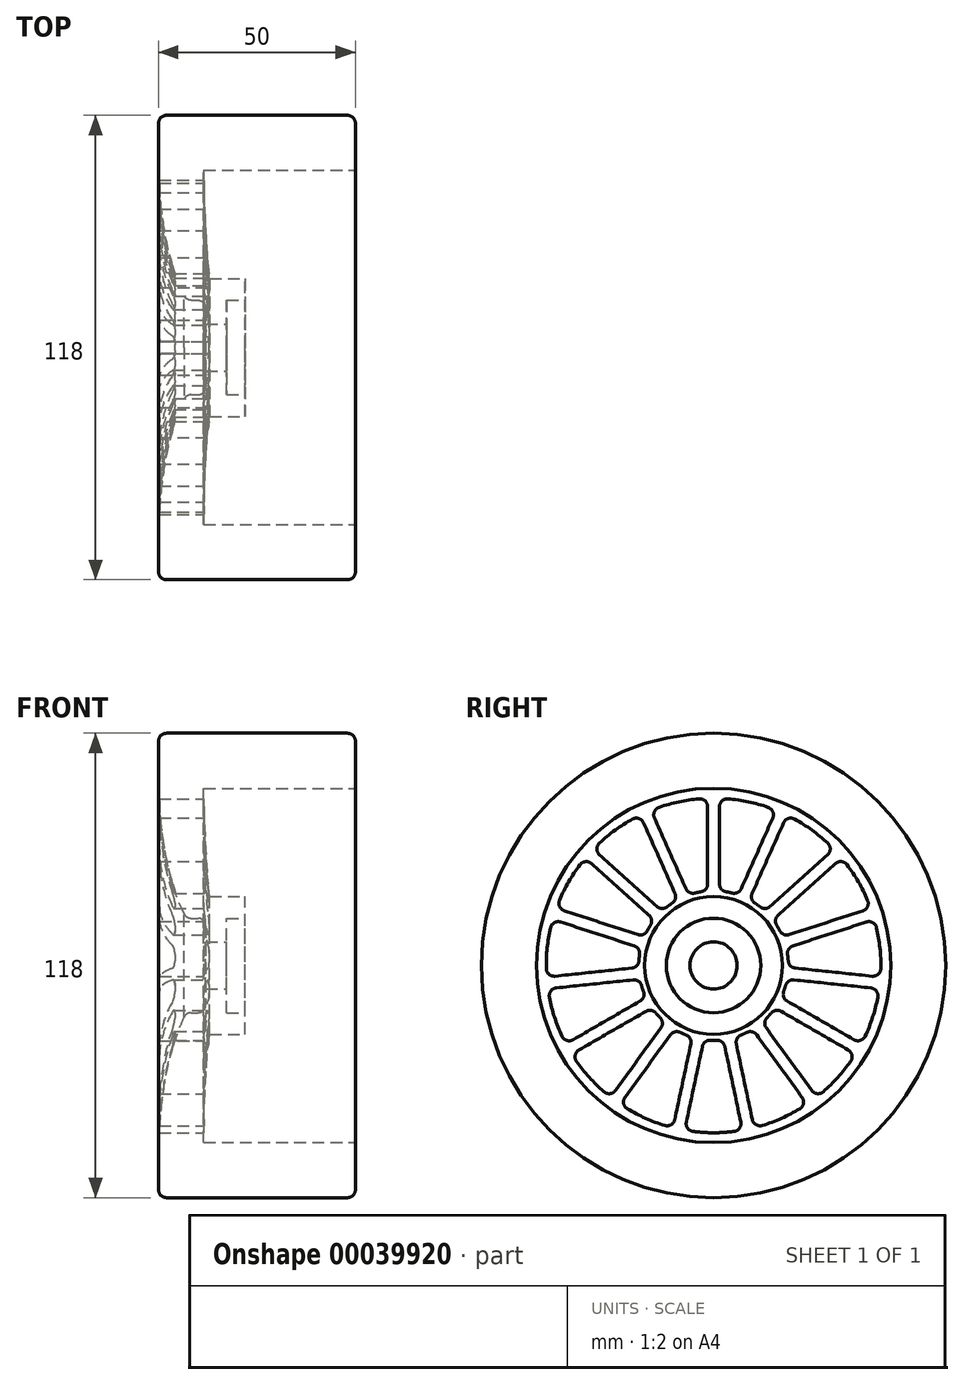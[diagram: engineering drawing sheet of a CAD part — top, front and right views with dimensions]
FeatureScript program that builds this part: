
annotation { "Feature Type Name" : "Feature", "Feature Type Description" : "" }
export const myFeature = defineFeature(function(context is Context, id is Id, definition is map)
    precondition{}
    {
        {
            var Q0;
            Q0=qCreatedBy(makeId("Right.planeOp"),FACE);
            var sketch = newSketch(context, id + "F0", { "sketchPlane" : qUnion([Q0]), "disableImprinting" : false});
            skCircle(sketch, "E0", {"center": v(0, 0) * mm, "radius": 59 * mm});
            skCircle(sketch, "E1", {"center": v(0, 0) * mm, "radius": 49 * mm});
            skSolve(sketch);
        }
        {
            var Q0;
            Q0=makeQuery(id+"F0.imprint","IMPRINT",FACE,{"disambiguationData":[TD([[makeQuery(id+"F0.imprint","IMPRINT",EDGE,{"derivedFrom":sQuery(id+"F0.wireOp",EDGE,"E0")}),1.0]])]});
            extrude(context, id + "F1", {"entities" : qUnion([Q0]), "oppositeDirection" : true, "depth" : 50 * mm});
        }
        {
            var Q0;
            Q0=qCreatedBy(makeId("Front.planeOp"),FACE);
            var sketch = newSketch(context, id + "F2", { "sketchPlane" : qUnion([Q0])});
            skLineSegment(sketch, "E2.bottom", {"start": v(0, 0) * mm, "end": v(-50, 0) * mm});
            skLineSegment(sketch, "E2.left", {"start": v(0, 0) * mm, "end": v(0, 49) * mm});
            skLineSegment(sketch, "E2.right", {"start": v(-50, 0) * mm, "end": v(-50, 49) * mm});
            skLineSegment(sketch, "E3", {"start": v(-50, 0) * mm, "end": v(-43, 0) * mm});
            skLineSegment(sketch, "E4", {"start": v(-50, 49) * mm, "end": v(0, 49) * mm});
            skLineSegment(sketch, "E5", {"start": v(0, 49) * mm, "end": v(0, 45) * mm});
            skLineSegment(sketch, "E6", {"start": v(-43, 0) * mm, "end": v(-43, 12) * mm, "construction": true});
            skLineSegment(sketch, "E7", {"start": v(-43, 12) * mm, "end": v(-38, 12) * mm});
            skFitSpline(sketch, "E8", {"points": [v(-43, 12) * mm, v(-50, 49) * mm], "startDerivative": vector(-8.6, 17.02) * mm, "endDerivative": vector(0, 58.5) * mm});
            skLineSegment(sketch, "E9", {"start": v(0, 45) * mm, "end": v(-38.53, 45) * mm});
            skLineSegment(sketch, "E10", {"start": v(0, 0) * mm, "end": v(0, 17.5) * mm});
            skLineSegment(sketch, "E11", {"start": v(0, 17.5) * mm, "end": v(-37, 17.5) * mm, "construction": true});
            skLineSegment(sketch, "E12", {"start": v(-38, 12) * mm, "end": v(-37, 12) * mm});
            skLineSegment(sketch, "E13", {"start": v(-37, 12) * mm, "end": v(-37, 17.5) * mm, "construction": true});
            skFitSpline(sketch, "E14", {"points": [v(-38.53, 45) * mm, v(-37, 17.5) * mm], "startDerivative": vector(0, -29.52) * mm, "endDerivative": vector(1.96, -9.49) * mm});
            skLineSegment(sketch, "E15", {"start": v(-38.53, 45) * mm, "end": v(-38.53, 35.16) * mm, "construction": true});
            skLineSegment(sketch, "E16", {"start": v(-38, 12) * mm, "end": v(-38, 6) * mm});
            skLineSegment(sketch, "E17", {"start": v(-38, 6) * mm, "end": v(-32.68, 6) * mm});
            skLineSegment(sketch, "E18", {"start": v(-32.68, 6) * mm, "end": v(-32.68, 12) * mm});
            skLineSegment(sketch, "E19", {"start": v(-32.68, 12) * mm, "end": v(-28.02, 12) * mm});
            skLineSegment(sketch, "E20", {"start": v(-28.02, 12) * mm, "end": v(-28.02, 17.5) * mm});
            skLineSegment(sketch, "E21", {"start": v(-28.02, 17.5) * mm, "end": v(-37, 17.5) * mm});
            skPoint(sketch, "E22.orphan", {"position": v(-50, 59) * mm});
            skPoint(sketch, "E23.orphan", {"position": v(0, 59) * mm});
            skSolve(sketch);
        }
        {
            var Q0;
            Q0=qCreatedBy(makeId("Front.planeOp"),FACE);
            var sketch = newSketch(context, id + "F3", { "sketchPlane" : qUnion([Q0])});
            skLineSegment(sketch, "E24", {"start": v(-51.75, 0) * mm, "end": v(-81.76, 0) * mm, "construction": true});
            skSolve(sketch);
        }
        {
            var Q0;
            Q0=makeQuery(id+"F2.imprint","IMPRINT",FACE,{"disambiguationData":[TD([[makeQuery(id+"F2.imprint","IMPRINT",EDGE,{"derivedFrom":sQuery(id+"F2.wireOp",EDGE,"E4")}),-1.0]])]});
            var Q1;
            Q1=sQuery(id+"F3.wireOp",EDGE,"E24");
            revolve(context, id + "F4", {"operationType" : NewBodyOperationType.ADD, "entities" : qUnion([Q0]), "axis" : qUnion([Q1]), "revolveType" : RevolveType.FULL});
        }
        {
            var Q0;
            Q0=makeQuery(id+"F1.opExtrude","CAP_EDGE",EDGE,{"disambiguationData":[OSD([sQuery(id+"F0.wireOp",EDGE,"E0")])],"isStart":false});
            var Q1;
            Q1=makeQuery(id+"F1.opExtrude","CAP_EDGE",EDGE,{"disambiguationData":[OSD([sQuery(id+"F0.wireOp",EDGE,"E0")])],"isStart":true});
            var Q2;
            Q2=makeQuery(id+"F4.opRevolve","SWEPT_EDGE",EDGE,{"disambiguationData":[OSD([sQuery(id+"F2.wireOp",EDGE,"E7"),sQuery(id+"F2.wireOp",EDGE,"E8")])]});
            var Q3;
            Q3=makeQuery(id+"F4.opRevolve","SWEPT_EDGE",EDGE,{"disambiguationData":[OSD([sQuery(id+"F2.wireOp",EDGE,"E7"),sQuery(id+"F2.wireOp",EDGE,"E16")])]});
            fillet(context, id + "F5", {"entities" : qUnion([Q0, Q1, Q2, Q3]), "radius" : 2 * mm, "tangentPropagation" : true, "allowEdgeOverflow" : false});
        }
        {
            var Q0;
            Q0=qCreatedBy(makeId("Right.planeOp"),FACE);
            var sketch = newSketch(context, id + "F6", { "sketchPlane" : qUnion([Q0])});
            skArc(sketch, "E25.0", {"start": v(-3.67, 42.34) * mm, "mid": v(-8.84, 41.57) * mm, "end": v(-13.87, 40.17) * mm});
            skLineSegment(sketch, "E25.1", {"start": v(-1.5, 20.7) * mm, "end": v(-1.5, 40.35) * mm});
            skArc(sketch, "E25.2", {"start": v(-3.17, 18.73) * mm, "mid": v(-3.95, 18.58) * mm, "end": v(-4.73, 18.4) * mm});
            skLineSegment(sketch, "E25.3", {"start": v(-7.05, 19.53) * mm, "end": v(-15.04, 37.47) * mm});
            skPoint(sketch, "E26.visualSharp", {"position": v(-1.5, 42.47) * mm});
            skArc(sketch, "E26.filletArc", {"start": v(-1.5, 40.35) * mm, "mid": v(-2.15, 41.82) * mm, "end": v(-3.67, 42.34) * mm});
            skPoint(sketch, "E27.visualSharp", {"position": v(-15.9, 39.41) * mm});
            skArc(sketch, "E27.filletArc", {"start": v(-13.87, 40.17) * mm, "mid": v(-15.05, 39.08) * mm, "end": v(-15.04, 37.47) * mm});
            skPoint(sketch, "E28.visualSharp", {"position": v(-6.33, 17.91) * mm});
            skArc(sketch, "E28.filletArc", {"start": v(-7.05, 19.53) * mm, "mid": v(-6.1, 18.54) * mm, "end": v(-4.73, 18.4) * mm});
            skPoint(sketch, "E29.visualSharp", {"position": v(-1.5, 18.94) * mm});
            skArc(sketch, "E29.filletArc", {"start": v(-3.17, 18.73) * mm, "mid": v(-1.97, 19.42) * mm, "end": v(-1.5, 20.7) * mm});
            skLineSegment(sketch, "E30.1.0", {"start": v(-9.8, 18.3) * mm, "end": v(-17.78, 36.25) * mm});
            skArc(sketch, "E30.1.1", {"start": v(-17.78, 36.25) * mm, "mid": v(-18.97, 37.33) * mm, "end": v(-20.58, 37.19) * mm});
            skArc(sketch, "E30.1.2", {"start": v(-20.58, 37.19) * mm, "mid": v(-24.98, 34.38) * mm, "end": v(-29, 31.06) * mm});
            skArc(sketch, "E30.1.3", {"start": v(-29, 31.06) * mm, "mid": v(-29.64, 29.58) * mm, "end": v(-28.98, 28.11) * mm});
            skLineSegment(sketch, "E30.1.4", {"start": v(-14.38, 14.97) * mm, "end": v(-28.98, 28.11) * mm});
            skArc(sketch, "E30.1.5", {"start": v(-14.38, 14.97) * mm, "mid": v(-13.1, 14.46) * mm, "end": v(-11.8, 14.89) * mm});
            skArc(sketch, "E30.1.6", {"start": v(-10.51, 15.83) * mm, "mid": v(-11.17, 15.37) * mm, "end": v(-11.8, 14.89) * mm});
            skArc(sketch, "E30.1.7", {"start": v(-10.51, 15.83) * mm, "mid": v(-9.7, 16.93) * mm, "end": v(-9.8, 18.3) * mm});
            skLineSegment(sketch, "E30.2.0", {"start": v(-16.4, 12.74) * mm, "end": v(-30.99, 25.88) * mm});
            skArc(sketch, "E30.2.1", {"start": v(-30.99, 25.88) * mm, "mid": v(-32.52, 26.39) * mm, "end": v(-33.92, 25.6) * mm});
            skArc(sketch, "E30.2.2", {"start": v(-33.92, 25.6) * mm, "mid": v(-36.8, 21.25) * mm, "end": v(-39.13, 16.58) * mm});
            skArc(sketch, "E30.2.3", {"start": v(-39.13, 16.58) * mm, "mid": v(-39.11, 14.97) * mm, "end": v(-37.91, 13.9) * mm});
            skLineSegment(sketch, "E30.2.4", {"start": v(-19.23, 7.83) * mm, "end": v(-37.91, 13.9) * mm});
            skArc(sketch, "E30.2.5", {"start": v(-19.23, 7.83) * mm, "mid": v(-17.86, 7.88) * mm, "end": v(-16.84, 8.8) * mm});
            skArc(sketch, "E30.2.6", {"start": v(-16.04, 10.18) * mm, "mid": v(-16.45, 9.5) * mm, "end": v(-16.84, 8.8) * mm});
            skArc(sketch, "E30.2.7", {"start": v(-16.04, 10.18) * mm, "mid": v(-15.75, 11.53) * mm, "end": v(-16.4, 12.74) * mm});
            skLineSegment(sketch, "E30.3.0", {"start": v(-20.16, 4.97) * mm, "end": v(-38.84, 11.04) * mm});
            skArc(sketch, "E30.3.1", {"start": v(-38.84, 11.04) * mm, "mid": v(-40.44, 10.88) * mm, "end": v(-41.4, 9.6) * mm});
            skArc(sketch, "E30.3.2", {"start": v(-41.4, 9.6) * mm, "mid": v(-42.27, 4.44) * mm, "end": v(-42.5, -0.77) * mm});
            skArc(sketch, "E30.3.3", {"start": v(-42.5, -0.77) * mm, "mid": v(-41.82, -2.24) * mm, "end": v(-40.28, -2.73) * mm});
            skLineSegment(sketch, "E30.3.4", {"start": v(-20.75, -0.67) * mm, "end": v(-40.28, -2.73) * mm});
            skArc(sketch, "E30.3.5", {"start": v(-20.75, -0.67) * mm, "mid": v(-19.52, -0.07) * mm, "end": v(-18.96, 1.2) * mm});
            skArc(sketch, "E30.3.6", {"start": v(-18.8, 2.78) * mm, "mid": v(-18.9, 1.99) * mm, "end": v(-18.96, 1.2) * mm});
            skArc(sketch, "E30.3.7", {"start": v(-18.8, 2.78) * mm, "mid": v(-19.07, 4.12) * mm, "end": v(-20.16, 4.97) * mm});
            skLineSegment(sketch, "E30.4.0", {"start": v(-20.44, -3.66) * mm, "end": v(-39.97, -5.7) * mm});
            skArc(sketch, "E30.4.1", {"start": v(-39.97, -5.7) * mm, "mid": v(-41.37, -6.5) * mm, "end": v(-41.73, -8.08) * mm});
            skArc(sketch, "E30.4.2", {"start": v(-41.73, -8.08) * mm, "mid": v(-40.42, -13.13) * mm, "end": v(-38.5, -17.99) * mm});
            skArc(sketch, "E30.4.3", {"start": v(-38.5, -17.99) * mm, "mid": v(-37.3, -19.05) * mm, "end": v(-35.7, -18.88) * mm});
            skLineSegment(sketch, "E30.4.4", {"start": v(-18.68, -9.05) * mm, "end": v(-35.7, -18.88) * mm});
            skArc(sketch, "E30.4.5", {"start": v(-18.68, -9.05) * mm, "mid": v(-17.8, -8) * mm, "end": v(-17.8, -6.62) * mm});
            skArc(sketch, "E30.4.6", {"start": v(-18.3, -5.1) * mm, "mid": v(-18.07, -5.87) * mm, "end": v(-17.8, -6.62) * mm});
            skArc(sketch, "E30.4.7", {"start": v(-18.3, -5.1) * mm, "mid": v(-19.1, -4) * mm, "end": v(-20.44, -3.66) * mm});
            skLineSegment(sketch, "E30.5.0", {"start": v(-17.18, -11.65) * mm, "end": v(-34.2, -21.47) * mm});
            skArc(sketch, "E30.5.1", {"start": v(-34.2, -21.47) * mm, "mid": v(-35.15, -22.77) * mm, "end": v(-34.83, -24.35) * mm});
            skArc(sketch, "E30.5.2", {"start": v(-34.83, -24.35) * mm, "mid": v(-31.58, -28.44) * mm, "end": v(-27.86, -32.1) * mm});
            skArc(sketch, "E30.5.3", {"start": v(-27.86, -32.1) * mm, "mid": v(-26.32, -32.57) * mm, "end": v(-24.93, -31.76) * mm});
            skLineSegment(sketch, "E30.5.4", {"start": v(-13.38, -15.87) * mm, "end": v(-24.93, -31.76) * mm});
            skArc(sketch, "E30.5.5", {"start": v(-13.38, -15.87) * mm, "mid": v(-13, -14.55) * mm, "end": v(-13.57, -13.3) * mm});
            skArc(sketch, "E30.5.6", {"start": v(-14.64, -12.1) * mm, "mid": v(-14.12, -12.71) * mm, "end": v(-13.57, -13.3) * mm});
            skArc(sketch, "E30.5.7", {"start": v(-14.64, -12.1) * mm, "mid": v(-15.83, -11.42) * mm, "end": v(-17.18, -11.65) * mm});
            skLineSegment(sketch, "E30.6.0", {"start": v(-10.96, -17.63) * mm, "end": v(-22.5, -33.52) * mm});
            skArc(sketch, "E30.6.1", {"start": v(-22.5, -33.52) * mm, "mid": v(-22.84, -35.1) * mm, "end": v(-21.92, -36.41) * mm});
            skArc(sketch, "E30.6.2", {"start": v(-21.92, -36.41) * mm, "mid": v(-17.29, -38.83) * mm, "end": v(-12.4, -40.65) * mm});
            skArc(sketch, "E30.6.3", {"start": v(-12.4, -40.65) * mm, "mid": v(-10.8, -40.46) * mm, "end": v(-9.86, -39.15) * mm});
            skLineSegment(sketch, "E30.6.4", {"start": v(-5.77, -19.94) * mm, "end": v(-9.86, -39.15) * mm});
            skArc(sketch, "E30.6.5", {"start": v(-5.77, -19.94) * mm, "mid": v(-5.97, -18.58) * mm, "end": v(-7, -17.67) * mm});
            skArc(sketch, "E30.6.6", {"start": v(-8.45, -17.02) * mm, "mid": v(-7.73, -17.36) * mm, "end": v(-7, -17.67) * mm});
            skArc(sketch, "E30.6.7", {"start": v(-8.45, -17.02) * mm, "mid": v(-9.82, -16.87) * mm, "end": v(-10.96, -17.63) * mm});
            skLineSegment(sketch, "E30.7.0", {"start": v(-2.84, -20.57) * mm, "end": v(-6.92, -39.78) * mm});
            skArc(sketch, "E30.7.1", {"start": v(-6.92, -39.78) * mm, "mid": v(-6.6, -41.36) * mm, "end": v(-5.21, -42.18) * mm});
            skArc(sketch, "E30.7.2", {"start": v(-5.21, -42.18) * mm, "mid": v(0, -42.5) * mm, "end": v(5.21, -42.18) * mm});
            skArc(sketch, "E30.7.3", {"start": v(5.21, -42.18) * mm, "mid": v(6.6, -41.36) * mm, "end": v(6.92, -39.78) * mm});
            skLineSegment(sketch, "E30.7.4", {"start": v(2.84, -20.57) * mm, "end": v(6.92, -39.78) * mm});
            skArc(sketch, "E30.7.5", {"start": v(2.84, -20.57) * mm, "mid": v(2.1, -19.4) * mm, "end": v(0.8, -18.98) * mm});
            skArc(sketch, "E30.7.6", {"start": v(-0.8, -18.98) * mm, "mid": v(0, -19) * mm, "end": v(0.8, -18.98) * mm});
            skArc(sketch, "E30.7.7", {"start": v(-0.8, -18.98) * mm, "mid": v(-2.1, -19.4) * mm, "end": v(-2.84, -20.57) * mm});
            skLineSegment(sketch, "E30.8.0", {"start": v(5.77, -19.94) * mm, "end": v(9.86, -39.15) * mm});
            skArc(sketch, "E30.8.1", {"start": v(9.86, -39.15) * mm, "mid": v(10.8, -40.46) * mm, "end": v(12.4, -40.65) * mm});
            skArc(sketch, "E30.8.2", {"start": v(12.4, -40.65) * mm, "mid": v(17.29, -38.83) * mm, "end": v(21.92, -36.41) * mm});
            skArc(sketch, "E30.8.3", {"start": v(21.92, -36.41) * mm, "mid": v(22.84, -35.1) * mm, "end": v(22.5, -33.52) * mm});
            skLineSegment(sketch, "E30.8.4", {"start": v(10.96, -17.63) * mm, "end": v(22.5, -33.52) * mm});
            skArc(sketch, "E30.8.5", {"start": v(10.96, -17.63) * mm, "mid": v(9.82, -16.87) * mm, "end": v(8.45, -17.02) * mm});
            skArc(sketch, "E30.8.6", {"start": v(7, -17.67) * mm, "mid": v(7.73, -17.36) * mm, "end": v(8.45, -17.02) * mm});
            skArc(sketch, "E30.8.7", {"start": v(7, -17.67) * mm, "mid": v(5.97, -18.58) * mm, "end": v(5.77, -19.94) * mm});
            skLineSegment(sketch, "E30.9.0", {"start": v(13.38, -15.87) * mm, "end": v(24.93, -31.76) * mm});
            skArc(sketch, "E30.9.1", {"start": v(24.93, -31.76) * mm, "mid": v(26.32, -32.57) * mm, "end": v(27.86, -32.1) * mm});
            skArc(sketch, "E30.9.2", {"start": v(27.86, -32.1) * mm, "mid": v(31.58, -28.44) * mm, "end": v(34.83, -24.35) * mm});
            skArc(sketch, "E30.9.3", {"start": v(34.83, -24.35) * mm, "mid": v(35.15, -22.77) * mm, "end": v(34.2, -21.47) * mm});
            skLineSegment(sketch, "E30.9.4", {"start": v(17.18, -11.65) * mm, "end": v(34.2, -21.47) * mm});
            skArc(sketch, "E30.9.5", {"start": v(17.18, -11.65) * mm, "mid": v(15.83, -11.42) * mm, "end": v(14.64, -12.1) * mm});
            skArc(sketch, "E30.9.6", {"start": v(13.57, -13.3) * mm, "mid": v(14.12, -12.71) * mm, "end": v(14.64, -12.1) * mm});
            skArc(sketch, "E30.9.7", {"start": v(13.57, -13.3) * mm, "mid": v(13, -14.55) * mm, "end": v(13.38, -15.87) * mm});
            skLineSegment(sketch, "E30.10.0", {"start": v(18.68, -9.05) * mm, "end": v(35.7, -18.88) * mm});
            skArc(sketch, "E30.10.1", {"start": v(35.7, -18.88) * mm, "mid": v(37.3, -19.05) * mm, "end": v(38.5, -17.99) * mm});
            skArc(sketch, "E30.10.2", {"start": v(38.5, -17.99) * mm, "mid": v(40.42, -13.13) * mm, "end": v(41.73, -8.08) * mm});
            skArc(sketch, "E30.10.3", {"start": v(41.73, -8.08) * mm, "mid": v(41.37, -6.5) * mm, "end": v(39.97, -5.7) * mm});
            skLineSegment(sketch, "E30.10.4", {"start": v(20.44, -3.66) * mm, "end": v(39.97, -5.7) * mm});
            skArc(sketch, "E30.10.5", {"start": v(20.44, -3.66) * mm, "mid": v(19.1, -4) * mm, "end": v(18.3, -5.1) * mm});
            skArc(sketch, "E30.10.6", {"start": v(17.8, -6.62) * mm, "mid": v(18.07, -5.87) * mm, "end": v(18.3, -5.1) * mm});
            skArc(sketch, "E30.10.7", {"start": v(17.8, -6.62) * mm, "mid": v(17.8, -8) * mm, "end": v(18.68, -9.05) * mm});
            skLineSegment(sketch, "E30.11.0", {"start": v(20.75, -0.67) * mm, "end": v(40.28, -2.73) * mm});
            skArc(sketch, "E30.11.1", {"start": v(40.28, -2.73) * mm, "mid": v(41.82, -2.24) * mm, "end": v(42.5, -0.77) * mm});
            skArc(sketch, "E30.11.2", {"start": v(42.5, -0.77) * mm, "mid": v(42.27, 4.44) * mm, "end": v(41.4, 9.6) * mm});
            skArc(sketch, "E30.11.3", {"start": v(41.4, 9.6) * mm, "mid": v(40.44, 10.88) * mm, "end": v(38.84, 11.04) * mm});
            skLineSegment(sketch, "E30.11.4", {"start": v(20.16, 4.97) * mm, "end": v(38.84, 11.04) * mm});
            skArc(sketch, "E30.11.5", {"start": v(20.16, 4.97) * mm, "mid": v(19.07, 4.12) * mm, "end": v(18.8, 2.78) * mm});
            skArc(sketch, "E30.11.6", {"start": v(18.96, 1.2) * mm, "mid": v(18.9, 1.99) * mm, "end": v(18.8, 2.78) * mm});
            skArc(sketch, "E30.11.7", {"start": v(18.96, 1.2) * mm, "mid": v(19.52, -0.07) * mm, "end": v(20.75, -0.67) * mm});
            skLineSegment(sketch, "E30.12.0", {"start": v(19.23, 7.83) * mm, "end": v(37.91, 13.9) * mm});
            skArc(sketch, "E30.12.1", {"start": v(37.91, 13.9) * mm, "mid": v(39.11, 14.97) * mm, "end": v(39.13, 16.58) * mm});
            skArc(sketch, "E30.12.2", {"start": v(39.13, 16.58) * mm, "mid": v(36.8, 21.25) * mm, "end": v(33.92, 25.6) * mm});
            skArc(sketch, "E30.12.3", {"start": v(33.92, 25.6) * mm, "mid": v(32.52, 26.39) * mm, "end": v(30.99, 25.88) * mm});
            skLineSegment(sketch, "E30.12.4", {"start": v(16.4, 12.74) * mm, "end": v(30.99, 25.88) * mm});
            skArc(sketch, "E30.12.5", {"start": v(16.4, 12.74) * mm, "mid": v(15.75, 11.53) * mm, "end": v(16.04, 10.18) * mm});
            skArc(sketch, "E30.12.6", {"start": v(16.84, 8.8) * mm, "mid": v(16.45, 9.5) * mm, "end": v(16.04, 10.18) * mm});
            skArc(sketch, "E30.12.7", {"start": v(16.84, 8.8) * mm, "mid": v(17.86, 7.88) * mm, "end": v(19.23, 7.83) * mm});
            skLineSegment(sketch, "E31.1.13.0", {"start": v(14.38, 14.97) * mm, "end": v(28.98, 28.11) * mm});
            skArc(sketch, "E31.3.13.0", {"start": v(28.98, 28.11) * mm, "mid": v(29.64, 29.58) * mm, "end": v(29, 31.06) * mm});
            skArc(sketch, "E31.7.13.0", {"start": v(29, 31.06) * mm, "mid": v(24.98, 34.38) * mm, "end": v(20.58, 37.19) * mm});
            skArc(sketch, "E31.11.13.0", {"start": v(20.58, 37.19) * mm, "mid": v(18.97, 37.33) * mm, "end": v(17.78, 36.25) * mm});
            skLineSegment(sketch, "E31.15.13.0", {"start": v(9.8, 18.3) * mm, "end": v(17.78, 36.25) * mm});
            skArc(sketch, "E31.18.13.0", {"start": v(9.8, 18.3) * mm, "mid": v(9.7, 16.93) * mm, "end": v(10.51, 15.83) * mm});
            skArc(sketch, "E31.22.13.0", {"start": v(11.8, 14.89) * mm, "mid": v(11.17, 15.37) * mm, "end": v(10.51, 15.83) * mm});
            skArc(sketch, "E31.26.13.0", {"start": v(11.8, 14.89) * mm, "mid": v(13.1, 14.46) * mm, "end": v(14.38, 14.97) * mm});
            skLineSegment(sketch, "E31.1.14.0", {"start": v(7.05, 19.53) * mm, "end": v(15.04, 37.47) * mm});
            skArc(sketch, "E31.3.14.0", {"start": v(15.04, 37.47) * mm, "mid": v(15.05, 39.08) * mm, "end": v(13.87, 40.17) * mm});
            skArc(sketch, "E31.7.14.0", {"start": v(13.87, 40.17) * mm, "mid": v(8.84, 41.57) * mm, "end": v(3.67, 42.34) * mm});
            skArc(sketch, "E31.11.14.0", {"start": v(3.67, 42.34) * mm, "mid": v(2.15, 41.82) * mm, "end": v(1.5, 40.35) * mm});
            skLineSegment(sketch, "E31.15.14.0", {"start": v(1.5, 20.7) * mm, "end": v(1.5, 40.35) * mm});
            skArc(sketch, "E31.18.14.0", {"start": v(1.5, 20.7) * mm, "mid": v(1.97, 19.42) * mm, "end": v(3.17, 18.73) * mm});
            skArc(sketch, "E31.22.14.0", {"start": v(4.73, 18.4) * mm, "mid": v(3.95, 18.58) * mm, "end": v(3.17, 18.73) * mm});
            skArc(sketch, "E31.26.14.0", {"start": v(4.73, 18.4) * mm, "mid": v(6.1, 18.54) * mm, "end": v(7.05, 19.53) * mm});
            skSolve(sketch);
        }
        {
            var Q0;
            Q0 = qSketchRegion(id + "F6", true);
            extrude(context, id + "F7", {"entities" : qUnion([Q0]), "operationType" : NewBodyOperationType.REMOVE, "endBound" : BoundingType.THROUGH_ALL, "oppositeDirection" : true, "depth" : 25 * mm});
        }
    });
